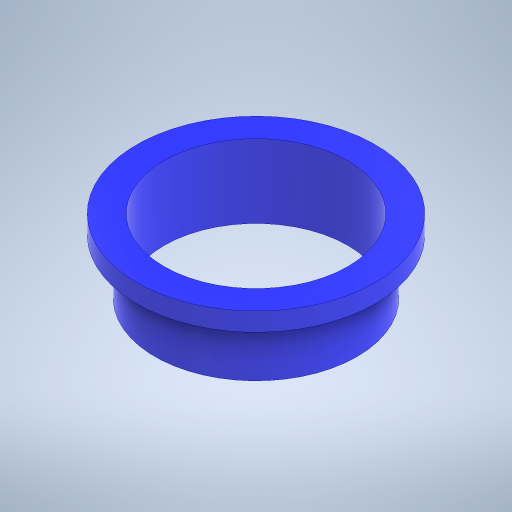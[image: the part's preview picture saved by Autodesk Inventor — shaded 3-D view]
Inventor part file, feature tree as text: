
AUTODESK INVENTOR PART (.ipt)
format: ipt  version: 2024 (Build 280153000, 153)  size: 254,976 bytes
history: native  units: mm
features: extrude x2, other x1, sketch x1
ambient origin geometry x8: Origin, YZ Plane, XZ Plane, XY Plane, X Axis, Y Axis, Z Axis, Center Point
bodies: Solid1 (feature_tree)
feature tree (4):
  extrude  "Extrusion1"  Depth=1.0mm
  extrude  "Extrusion2"  Depth=3.0mm TaperAngle=0.0deg
  other  "Work Point1"
  sketch  "Sketch2"  dims[d0=10.0mm d1=11.0mm d2=3.0mm d3=0.0mm d4=13.0mm d5=1.0mm d6=0.0mm]
